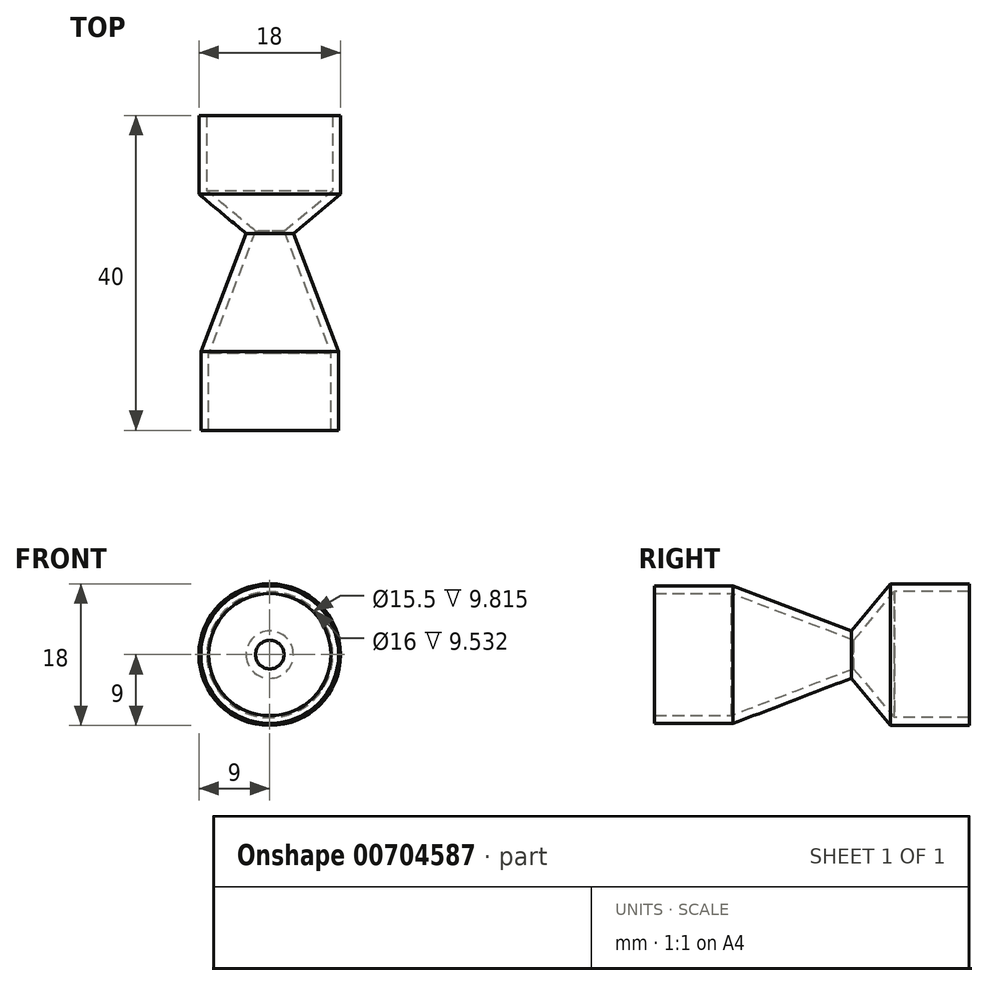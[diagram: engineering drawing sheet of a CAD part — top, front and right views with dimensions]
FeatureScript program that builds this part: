
annotation { "Feature Type Name" : "Feature", "Feature Type Description" : "" }
export const myFeature = defineFeature(function(context is Context, id is Id, definition is map)
    precondition{}
    {
        {
            var Q0;
            Q0=qCreatedBy(makeId("Front.planeOp"),FACE);
            var sketch = newSketch(context, id + "F0", { "sketchPlane" : qUnion([Q0])});
            skCircle(sketch, "E0", {"center": v(0, 0) * mm, "radius": 8.75 * mm});
            skLineSegment(sketch, "E1", {"start": v(0, 8.75) * mm, "end": v(0, -8.75) * mm, "construction": true});
            skSolve(sketch);
        }
        {
            var Q0;
            Q0=sQuery(id+"F0.wireOp",EDGE,"E1");
            cPlane(context, id + "F1", {"entities" : qUnion([Q0]), "cplaneType" : CPlaneType.LINE_ANGLE, "offset" : 25 * mm, "angle" : 0 * degree, "width" : 150 * mm, "height" : 150 * mm});
        }
        {
            var Q0;
            Q0=qCreatedBy(id+"F1.planeOp",FACE);
            var sketch = newSketch(context, id + "F2", { "sketchPlane" : qUnion([Q0])});
            skLineSegment(sketch, "E2", {"start": v(0, 0) * mm, "end": v(-15, 0) * mm});
            skLineSegment(sketch, "E3", {"start": v(-15, -3) * mm, "end": v(-15, 3) * mm, "construction": true});
            skSolve(sketch);
        }
        {
            var Q0;
            Q0=sQuery(id+"F2.wireOp",EDGE,"E3");
            cPlane(context, id + "F3", {"entities" : qUnion([Q0]), "cplaneType" : CPlaneType.LINE_ANGLE, "offset" : 25 * mm, "angle" : 90 * degree, "width" : 150 * mm, "height" : 150 * mm});
        }
        {
            var Q0;
            Q0=qCreatedBy(id+"F3.planeOp",FACE);
            var sketch = newSketch(context, id + "F4", { "sketchPlane" : qUnion([Q0])});
            skPoint(sketch, "E4.0", {"position": v(0, 0) * mm});
            skPoint(sketch, "E5.0", {"position": v(0, 3) * mm});
            skCircle(sketch, "E6", {"center": v(0, 0) * mm, "radius": 3 * mm});
            skSolve(sketch);
        }
        {
            var Q0;
            Q0=makeQuery(id+"F0.imprint","IMPRINT",FACE,{"disambiguationData":[TD([[makeQuery(id+"F0.imprint","IMPRINT",EDGE,{"derivedFrom":sQuery(id+"F0.wireOp",EDGE,"E0")}),1.0]])]});
            var Q1;
            Q1=makeQuery(id+"F4.imprint","IMPRINT",FACE,{"disambiguationData":[TD([[makeQuery(id+"F4.imprint","IMPRINT",EDGE,{"derivedFrom":sQuery(id+"F4.wireOp",EDGE,"E6")}),1.0]])]});
            loft(context, id + "F5", {"sheetProfilesArray" : [{ "sheetProfileEntities" : qUnion([Q0]) }, { "sheetProfileEntities" : qUnion([Q1]) }]});
        }
        {
            var Q0;
            Q0=makeQuery(id+"F5.opLoft","CAP_FACE",FACE,{"disambiguationData":[OSD([makeQuery(id+"F0.imprint","IMPRINT",FACE,{"disambiguationData":[TD([[makeQuery(id+"F0.imprint","IMPRINT",EDGE,{"derivedFrom":sQuery(id+"F0.wireOp",EDGE,"E0")}),1.0]])]})])],"isStart":true});
            extrude(context, id + "F6", {"entities" : qUnion([Q0]), "operationType" : NewBodyOperationType.ADD, "depth" : 10 * mm, "offsetDistance" : 25 * mm});
        }
        {
            var Q0;
            Q0=sQuery(id+"F2.wireOp",EDGE,"E3");
            cPlane(context, id + "F7", {"entities" : qUnion([Q0]), "cplaneType" : CPlaneType.LINE_ANGLE, "offset" : 25 * mm, "angle" : 0 * degree, "width" : 150 * mm, "height" : 150 * mm});
        }
        {
            var Q0;
            Q0=qCreatedBy(id+"F7.planeOp",FACE);
            var sketch = newSketch(context, id + "F8", { "sketchPlane" : qUnion([Q0])});
            skPoint(sketch, "E7.0", {"position": v(15, 0) * mm});
            skLineSegment(sketch, "E8", {"start": v(15, 0) * mm, "end": v(20, 0) * mm});
            skLineSegment(sketch, "E9", {"start": v(20, 9) * mm, "end": v(20, -9) * mm});
            skSolve(sketch);
        }
        {
            var Q0;
            Q0=sQuery(id+"F8.wireOp",EDGE,"E9");
            cPlane(context, id + "F9", {"entities" : qUnion([Q0]), "cplaneType" : CPlaneType.LINE_ANGLE, "offset" : 25 * mm, "angle" : 90 * degree, "width" : 150 * mm, "height" : 150 * mm});
        }
        {
            var Q0;
            Q0=qCreatedBy(id+"F9.planeOp",FACE);
            var sketch = newSketch(context, id + "F10", { "sketchPlane" : qUnion([Q0])});
            skPoint(sketch, "E10.0", {"position": v(0, 0) * mm});
            skPoint(sketch, "E11.0", {"position": v(0, 9) * mm});
            skCircle(sketch, "E12", {"center": v(0, 0) * mm, "radius": 9 * mm});
            skSolve(sketch);
        }
        {
            var Q1;
            Q1=makeQuery(id+"F10.imprint","IMPRINT",FACE,{"disambiguationData":[TD([[makeQuery(id+"F10.imprint","IMPRINT",EDGE,{"derivedFrom":sQuery(id+"F10.wireOp",EDGE,"E12")}),1.0]])]});
            var Q2;
            Q2=makeQuery(id+"F5.opLoft","CAP_FACE",FACE,{"disambiguationData":[OSD([makeQuery(id+"F4.imprint","IMPRINT",FACE,{"disambiguationData":[TD([[makeQuery(id+"F4.imprint","IMPRINT",EDGE,{"derivedFrom":sQuery(id+"F4.wireOp",EDGE,"E6")}),1.0]])]})])],"isStart":true});
            loft(context, id + "F11", {"operationType" : NewBodyOperationType.ADD, "sheetProfilesArray" : [{ "sheetProfileEntities" : qUnion([Q1]) }, { "sheetProfileEntities" : qUnion([Q2]) }]});
        }
        {
            var Q0;
            Q0=makeQuery(id+"F11.opLoft","CAP_FACE",FACE,{"disambiguationData":[OSD([makeQuery(id+"F10.imprint","IMPRINT",FACE,{"disambiguationData":[TD([[makeQuery(id+"F10.imprint","IMPRINT",EDGE,{"derivedFrom":sQuery(id+"F10.wireOp",EDGE,"E12")}),1.0]])]})])],"isStart":true});
            extrude(context, id + "F12", {"entities" : qUnion([Q0]), "operationType" : NewBodyOperationType.ADD, "depth" : 10 * mm, "offsetDistance" : 25 * mm});
        }
        {
            var Q0;
            Q0=makeQuery(id+"F6.opExtrude","CAP_FACE",FACE,{"disambiguationData":[OSD([makeQuery(id+"F0.imprint","IMPRINT",FACE,{"disambiguationData":[TD([[makeQuery(id+"F0.imprint","IMPRINT",EDGE,{"derivedFrom":sQuery(id+"F0.wireOp",EDGE,"E0")}),1.0]])]})])],"isStart":false});
            var Q1;
            Q1=makeQuery(id+"F12.opExtrude","CAP_FACE",FACE,{"disambiguationData":[OSD([makeQuery(id+"F10.imprint","IMPRINT",FACE,{"disambiguationData":[TD([[makeQuery(id+"F10.imprint","IMPRINT",EDGE,{"derivedFrom":sQuery(id+"F10.wireOp",EDGE,"E12")}),1.0]])]})])],"isStart":false});
            shell(context, id + "F13", {"entities" : qUnion([Q0, Q1]), "thickness" : 1 * mm});
        }
    });
